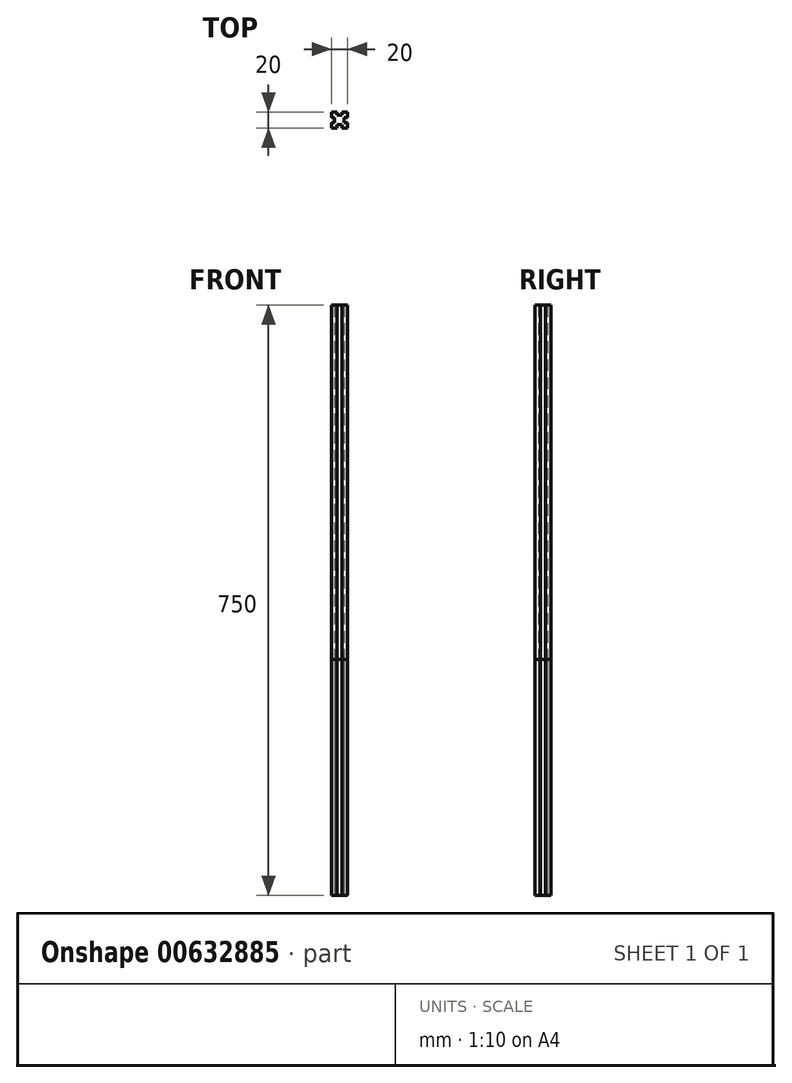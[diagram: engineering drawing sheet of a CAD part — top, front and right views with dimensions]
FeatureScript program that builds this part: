
annotation { "Feature Type Name" : "Feature", "Feature Type Description" : "" }
export const myFeature = defineFeature(function(context is Context, id is Id, definition is map)
    precondition{}
    {
        {
            var Q0;
            Q0=qCreatedBy(makeId("Top.planeOp"),FACE);
            var sketch = newSketch(context, id + "F0", { "sketchPlane" : qUnion([Q0])});
            skLineSegment(sketch, "E0.bottom", {"start": v(10, -10) * mm, "end": v(3, -10) * mm});
            skLineSegment(sketch, "E0.top", {"start": v(10, 10) * mm, "end": v(3, 10) * mm});
            skLineSegment(sketch, "E0.left", {"start": v(10, -10) * mm, "end": v(10, -3) * mm});
            skLineSegment(sketch, "E0.right", {"start": v(-10, -10) * mm, "end": v(-10, -3) * mm});
            skPoint(sketch, "E0.middle", {"position": v(0, 0) * mm});
            skLineSegment(sketch, "E1.bottom", {"start": v(10, -3) * mm, "end": v(6, -3) * mm});
            skLineSegment(sketch, "E1.top", {"start": v(10, 3) * mm, "end": v(6, 3) * mm});
            skLineSegment(sketch, "E2.left", {"start": v(3, -10) * mm, "end": v(3, -6) * mm});
            skLineSegment(sketch, "E2.right", {"start": v(-3, -10) * mm, "end": v(-3, -6) * mm});
            skLineSegment(sketch, "E3.0", {"start": v(3, 6) * mm, "end": v(-3, 6) * mm});
            skLineSegment(sketch, "E4.0", {"start": v(6, -3) * mm, "end": v(6, 3) * mm});
            skLineSegment(sketch, "E5.0", {"start": v(3, -6) * mm, "end": v(-3, -6) * mm});
            skLineSegment(sketch, "E6.0", {"start": v(-6, -3) * mm, "end": v(-6, 3) * mm});
            skLineSegment(sketch, "E7.trimOffspring", {"start": v(-6, 3) * mm, "end": v(-10, 3) * mm});
            skLineSegment(sketch, "E8.trimOffspring", {"start": v(-3, 6) * mm, "end": v(-3, 10) * mm});
            skLineSegment(sketch, "E9.trimOffspring", {"start": v(3, 6) * mm, "end": v(3, 10) * mm});
            skLineSegment(sketch, "E10.trimOffspring", {"start": v(-6, -3) * mm, "end": v(-10, -3) * mm});
            skLineSegment(sketch, "E11.trimOffspring", {"start": v(10, 3) * mm, "end": v(10, 10) * mm});
            skLineSegment(sketch, "E12.trimOffspring", {"start": v(-3, 10) * mm, "end": v(-10, 10) * mm});
            skLineSegment(sketch, "E13.trimOffspring", {"start": v(-10, 3) * mm, "end": v(-10, 10) * mm});
            skLineSegment(sketch, "E14.trimOffspring", {"start": v(-3, -10) * mm, "end": v(-10, -10) * mm});
            skSolve(sketch);
        }
        {
            var Q0;
            Q0=qSketchRegion(id+"F0",true);
            extrude(context, id + "F1", {"entities" : qUnion([Q0]), "depth" : 750 * mm});
        }
        {
            var Q0;
            Q0=makeQuery(id+"F0.imprint","IMPRINT",FACE,{"disambiguationData":[TD([[makeQuery(id+"F0.imprint","IMPRINT",EDGE,{"derivedFrom":sQuery(id+"F0.wireOp",EDGE,"E0.bottom")}),-1.0]])]});
            extrude(context, id + "F2", {"entities" : qUnion([Q0]), "depth" : 300 * mm});
        }
    });
